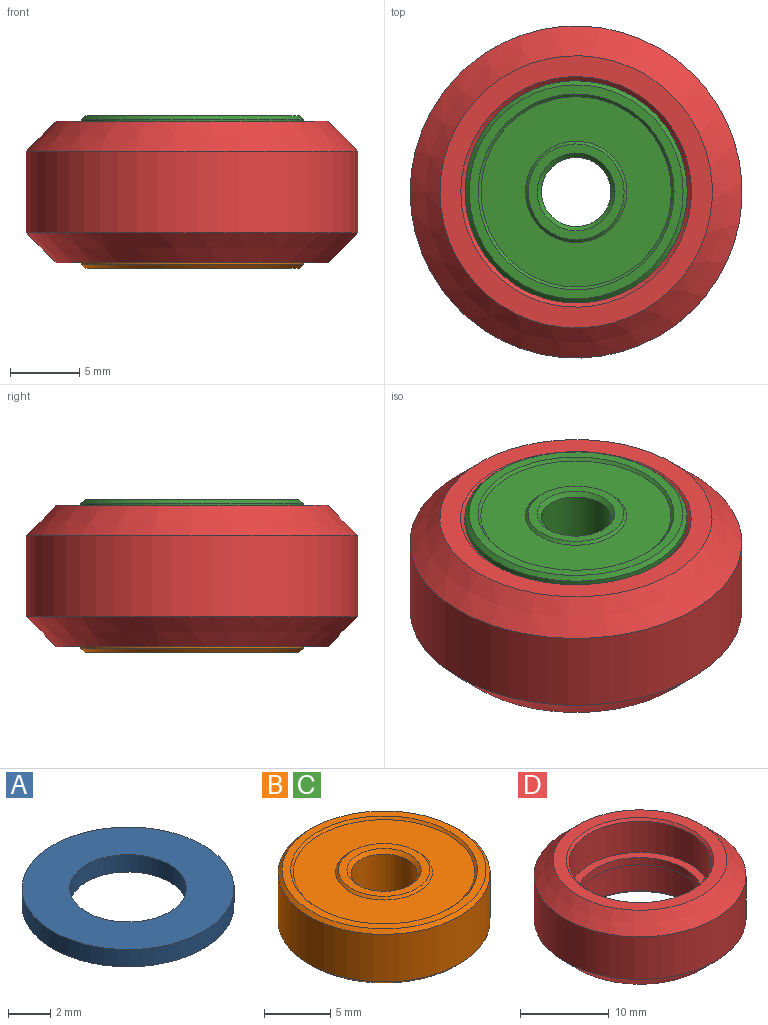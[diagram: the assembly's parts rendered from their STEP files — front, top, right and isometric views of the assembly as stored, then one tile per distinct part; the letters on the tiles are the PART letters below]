
ASSEMBLY  parts=4 mates=3
PART A: 4 faces, bbox 10x10x1 mm
  f0: cylinder r=2.75mm len=5.5mm, axis (0,0,-1), area 17.3mm2, adj f2,f3
  f1: cylinder r=5mm len=10mm, axis (0,0,-1), area 31.4mm2, adj f2,f3
  f2: plane 10x10mm, normal (0,0,1), area 54.8mm2, adj f0,f1
  f3: plane 10x10mm, normal (0,0,-1), area 54.8mm2, adj f0,f1
PART B: 16 faces, bbox 16x16x5 mm
  f0: plane 13.7x13.7mm, normal (0,0,1), area 105.6mm2, adj f13,f14
  f1: plane 13.7x13.7mm, normal (0,0,-1), area 105.6mm2, adj f9,f10
  f2: cylinder r=2.5mm len=5mm, axis (0,0,-1), area 69.1mm2, adj f8,f12
  f3: plane 6.9x6.9mm, normal (0,0,1), area 12.8mm2, adj f12,f13
  f4: plane 6.9x6.9mm, normal (0,0,-1), area 12.8mm2, adj f8,f9
  f5: cylinder r=8mm len=16mm, axis (0,0,-1), area 221.2mm2, adj f11,f15
  f6: plane 15.4x15.4mm, normal (0,0,1), area 30.1mm2, adj f14,f15
  f7: plane 15.4x15.4mm, normal (0,0,-1), area 30.1mm2, adj f10,f11
  f8: cone r=2.8mm half-angle=45deg, axis (0,0,-1), area 7.1mm2, adj f2,f4
  f9: cone r=3.75mm half-angle=45deg, axis (0,0,1), area 6.3mm2, adj f1,f4
  f10: cone r=7.05mm half-angle=45deg, axis (0,0,-1), area 12.4mm2, adj f1,f7
  f11: cone r=8mm half-angle=45deg, axis (0,0,1), area 20.9mm2, adj f5,f7
  f12: cone r=2.5mm half-angle=45deg, axis (0,0,1), area 7.1mm2, adj f2,f3
  f13: cone r=3.45mm half-angle=45deg, axis (0,0,-1), area 6.3mm2, adj f0,f3
  f14: cone r=6.75mm half-angle=45deg, axis (0,0,1), area 12.4mm2, adj f0,f6
  f15: cone r=7.7mm half-angle=45deg, axis (0,0,-1), area 20.9mm2, adj f5,f6
PART C: same geometry as B
PART D: 12 faces, bbox 23.9x23.9x10.2 mm
  f0: cylinder r=8mm len=16mm, axis (0,0,-1), area 216.1mm2, adj f1,f11
  f1: plane 16x16mm, normal (0,0,-1), area 47.1mm2, adj f0,f2
  f2: cylinder r=7mm len=14mm, axis (0,0,-1), area 44mm2, adj f1,f3
  f3: plane 16x16mm, normal (0,0,1), area 47.1mm2, adj f2,f4
  f4: cylinder r=8mm len=16mm, axis (0,0,-1), area 216.1mm2, adj f3,f5
  f5: cone r=8.3mm half-angle=45deg, axis (0,0,1), area 21.7mm2, adj f4,f6
  f6: plane 19.6x19.6mm, normal (0,0,1), area 85.3mm2, adj f5,f7
  f7: cone r=9.8mm half-angle=45deg, axis (0,0,-1), area 207.8mm2, adj f6,f8
  f8: cylinder r=11.95mm len=23.9mm, axis (0,0,-1), area 443mm2, adj f7,f9
  f9: cone r=11.95mm half-angle=45deg, axis (0,0,1), area 207.8mm2, adj f8,f10
  f10: plane 19.6x19.6mm, normal (0,0,-1), area 85.3mm2, adj f9,f11
  f11: cone r=8.3mm half-angle=45deg, axis (0,0,-1), area 21.7mm2, adj f0,f10
PLACE A t=(0,0,-0.5)mm
PLACE B t=(0,0,-5.5)mm
PLACE C t=(0,0,0.5)mm
PLACE D at identity fixed
MATE fastened D.f0 <-> B.f2  axis (0,0,-1) through (0,0,-0.5)mm
MATE fastened D.f0 <-> C.f2  axis (0,0,1) through (0,0,0.5)mm
MATE fastened D.f0 <-> A.f0  axis (0,0,1) through (0,0,0.5)mm
